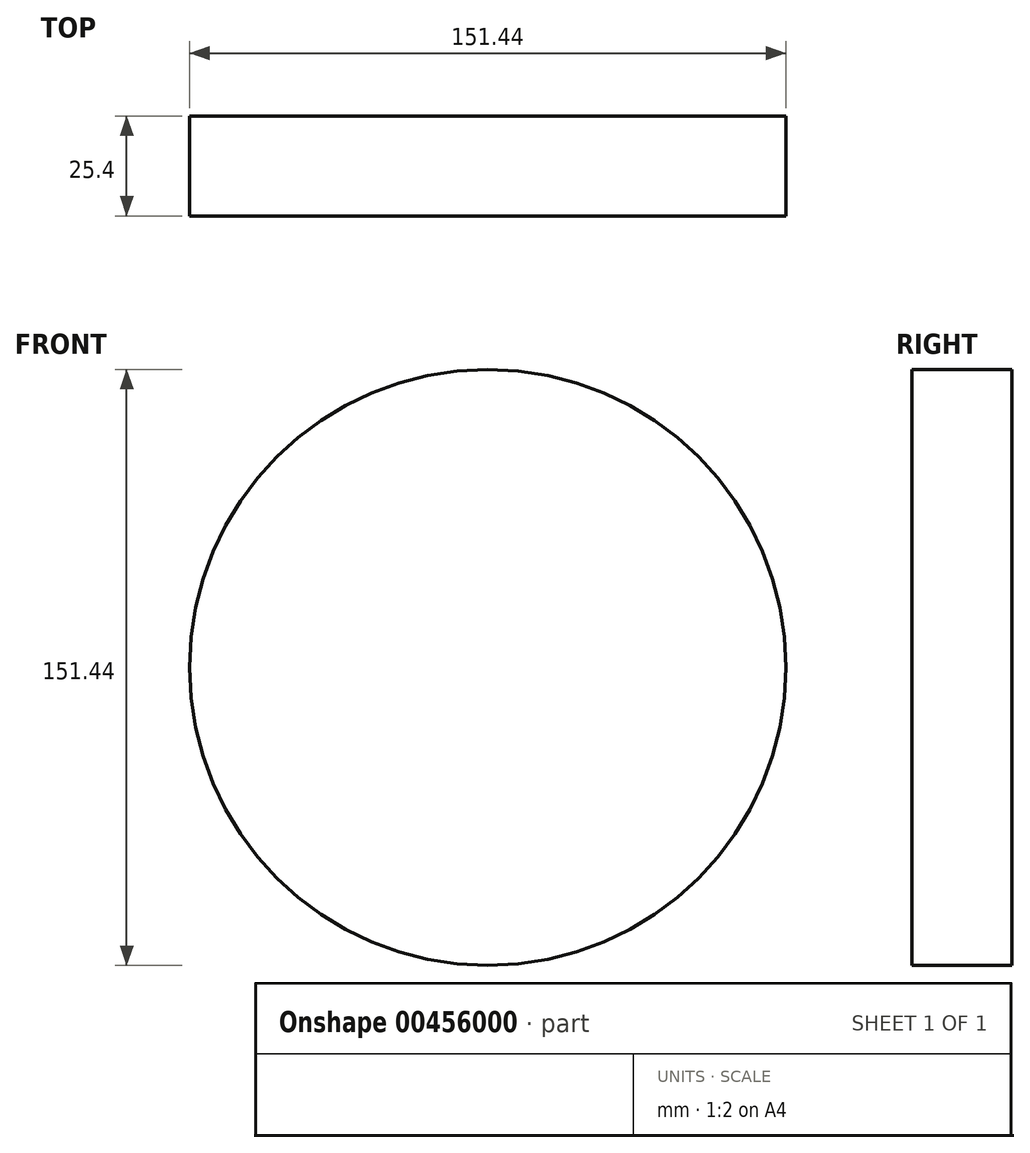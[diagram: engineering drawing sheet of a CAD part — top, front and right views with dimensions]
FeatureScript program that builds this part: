
annotation { "Feature Type Name" : "Feature", "Feature Type Description" : "" }
export const myFeature = defineFeature(function(context is Context, id is Id, definition is map)
    precondition{}
    {
        {
            var Q0;
            Q0=qCreatedBy(makeId("Front.planeOp"),FACE);
            var sketch = newSketch(context, id + "F0", { "sketchPlane" : qUnion([Q0])});
            skCircle(sketch, "E0", {"center": v(0, 0) * mm, "radius": 75.72 * mm});
            skSolve(sketch);
        }
        {
            var Q0;
            Q0 = qSketchRegion(id + "F0", true);
            extrude(context, id + "F1", {"entities" : qUnion([Q0]), "depth" : 25.4 * mm});
        }
    });
